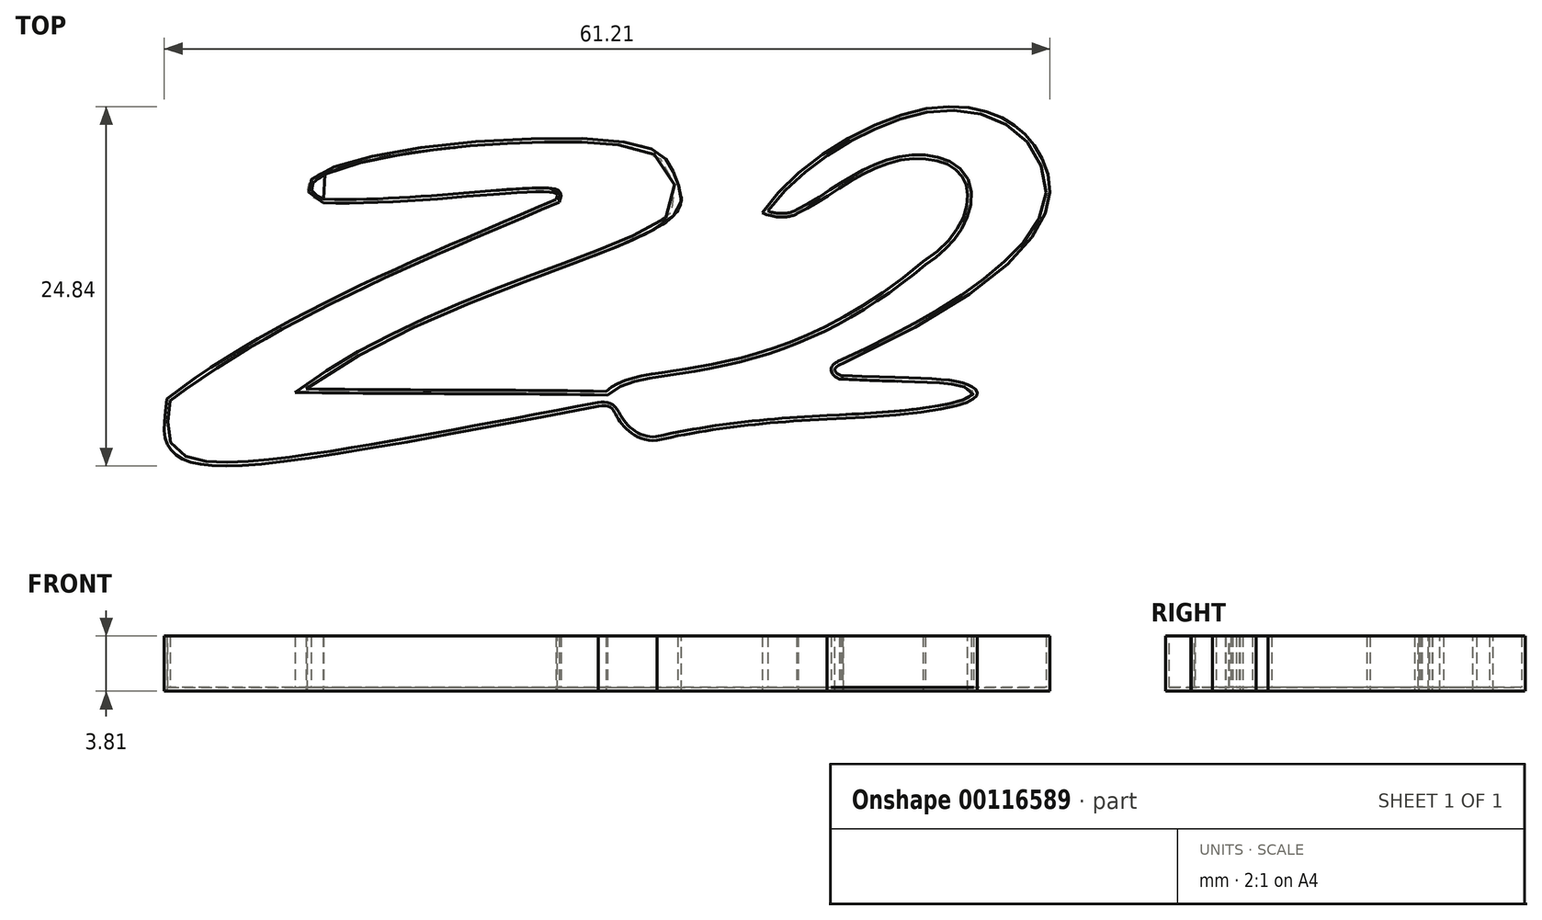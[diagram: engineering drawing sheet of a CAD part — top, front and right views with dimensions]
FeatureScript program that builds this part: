
annotation { "Feature Type Name" : "Feature", "Feature Type Description" : "" }
export const myFeature = defineFeature(function(context is Context, id is Id, definition is map)
    precondition{}
    {
        {
            var Q0;
            Q0=qCreatedBy(makeId("Top.planeOp"),FACE);
            var sketch = newSketch(context, id + "F0", { "sketchPlane" : qUnion([Q0])});
            skSolve(sketch);
        }
        {
            var Q0;
            Q0=qCreatedBy(makeId("Top.planeOp"),FACE);
            var sketch = newSketch(context, id + "F1", { "sketchPlane" : qUnion([Q0])});
            skFitSpline(sketch, "E0", {"points": [v(-39.21, 43.8) * mm, v(-66.12, 30.02) * mm], "startDerivative": vector(-27.83, -11.84) * mm, "endDerivative": vector(-22.17, -17) * mm});
            skFitSpline(sketch, "E1", {"points": [v(-39.21, 43.8) * mm, v(-39.21, 44.21) * mm, v(-55.33, 43.59) * mm], "startDerivative": vector(1.52, 4.04) * mm, "endDerivative": vector(-19.68, 1.04) * mm});
            skFitSpline(sketch, "E2", {"points": [v(-55.33, 43.59) * mm, v(-56, 45.3) * mm, v(-33.46, 47.57) * mm, v(-31.03, 45.46) * mm, v(-30.87, 42.95) * mm, v(-56.48, 30.71) * mm], "startDerivative": vector(-35.32, 11.99) * mm, "endDerivative": vector(-79.12, -56.6) * mm});
            skFitSpline(sketch, "E3", {"points": [v(-56.48, 30.71) * mm, v(-35.75, 30.54) * mm], "startDerivative": vector(20.3, -0.38) * mm, "endDerivative": vector(20.3, -0.38) * mm});
            skFitSpline(sketch, "E4", {"points": [v(-66.12, 30.02) * mm, v(-66.12, 26.98) * mm, v(-64.84, 25.78) * mm, v(-36.29, 29.51) * mm], "startDerivative": vector(-2.78, -21.5) * mm, "endDerivative": vector(91.79, 17.45) * mm});
            skFitSpline(sketch, "E5", {"points": [v(-35.75, 30.54) * mm, v(-13.84, 39.5) * mm], "startDerivative": vector(7.6, 7.47) * mm, "endDerivative": vector(32.96, 27.62) * mm});
            skFitSpline(sketch, "E6", {"points": [v(-13.84, 39.5) * mm, v(-11.07, 45.26) * mm, v(-15.97, 46.38) * mm, v(-22.48, 42.86) * mm], "startDerivative": vector(24.34, 15.3) * mm, "endDerivative": vector(-13.8, -6.13) * mm});
            skFitSpline(sketch, "E7", {"points": [v(-24.98, 42.86) * mm, v(-14.1, 49.98) * mm, v(-8.12, 49.3) * mm, v(-5.8, 46.93) * mm, v(-19.4, 32.47) * mm], "startDerivative": vector(21.56, 33.1) * mm, "endDerivative": vector(-131.1, -60.48) * mm});
            skFitSpline(sketch, "E8", {"points": [v(-19.4, 32.47) * mm, v(-19.4, 31.64) * mm], "startDerivative": vector(-4.17, -1.53) * mm, "endDerivative": vector(-0.84, 0.61) * mm});
            skFitSpline(sketch, "E9", {"points": [v(-19.4, 31.64) * mm, v(-10.74, 31) * mm, v(-20.48, 28.63) * mm], "startDerivative": vector(32.3, -1.63) * mm, "endDerivative": vector(-65.35, -2.55) * mm});
            skFitSpline(sketch, "E10", {"points": [v(-20.48, 28.63) * mm, v(-32.25, 27.16) * mm], "startDerivative": vector(-13.98, -0.76) * mm, "endDerivative": vector(-11.27, -2.52) * mm});
            skFitSpline(sketch, "E11", {"points": [v(-36.29, 29.51) * mm, v(-34.97, 28.73) * mm, v(-32.25, 27.16) * mm], "startDerivative": vector(6.87, 1.07) * mm, "endDerivative": vector(6.81, 0.77) * mm});
            skFitSpline(sketch, "E12", {"points": [v(-24.98, 42.86) * mm, v(-22.48, 42.86) * mm], "startDerivative": vector(3.7, -1.43) * mm, "endDerivative": vector(1.37, 0.83) * mm});
            skSolve(sketch);
        }
        {
            var Q0;
            Q0 = qSketchRegion(id + "F1", true);
            var Q1;
            Q1 = qSketchRegion(id + "F0", true);
            extrude(context, id + "F2", {"entities" : qUnion([Q0, Q1]), "depth" : 3.8 * mm});
        }
        {
            var Q0;
            Q0=makeQuery(id+"F2.opExtrude","CAP_FACE",FACE,{"disambiguationData":[OSD([sQuery(id+"F1.wireOp",EDGE,"E0"),sQuery(id+"F1.wireOp",EDGE,"E1"),sQuery(id+"F1.wireOp",EDGE,"E2"),sQuery(id+"F1.wireOp",EDGE,"E3"),sQuery(id+"F1.wireOp",EDGE,"E4"),sQuery(id+"F1.wireOp",EDGE,"E5"),sQuery(id+"F1.wireOp",EDGE,"E6"),sQuery(id+"F1.wireOp",EDGE,"E7"),sQuery(id+"F1.wireOp",EDGE,"E8"),sQuery(id+"F1.wireOp",EDGE,"E9"),sQuery(id+"F1.wireOp",EDGE,"E10"),sQuery(id+"F1.wireOp",EDGE,"E11"),sQuery(id+"F1.wireOp",EDGE,"E12")])],"isStart":false});
            shell(context, id + "F3", {"entities" : qUnion([Q0]), "thickness" : 0.25 * mm});
        }
    });
